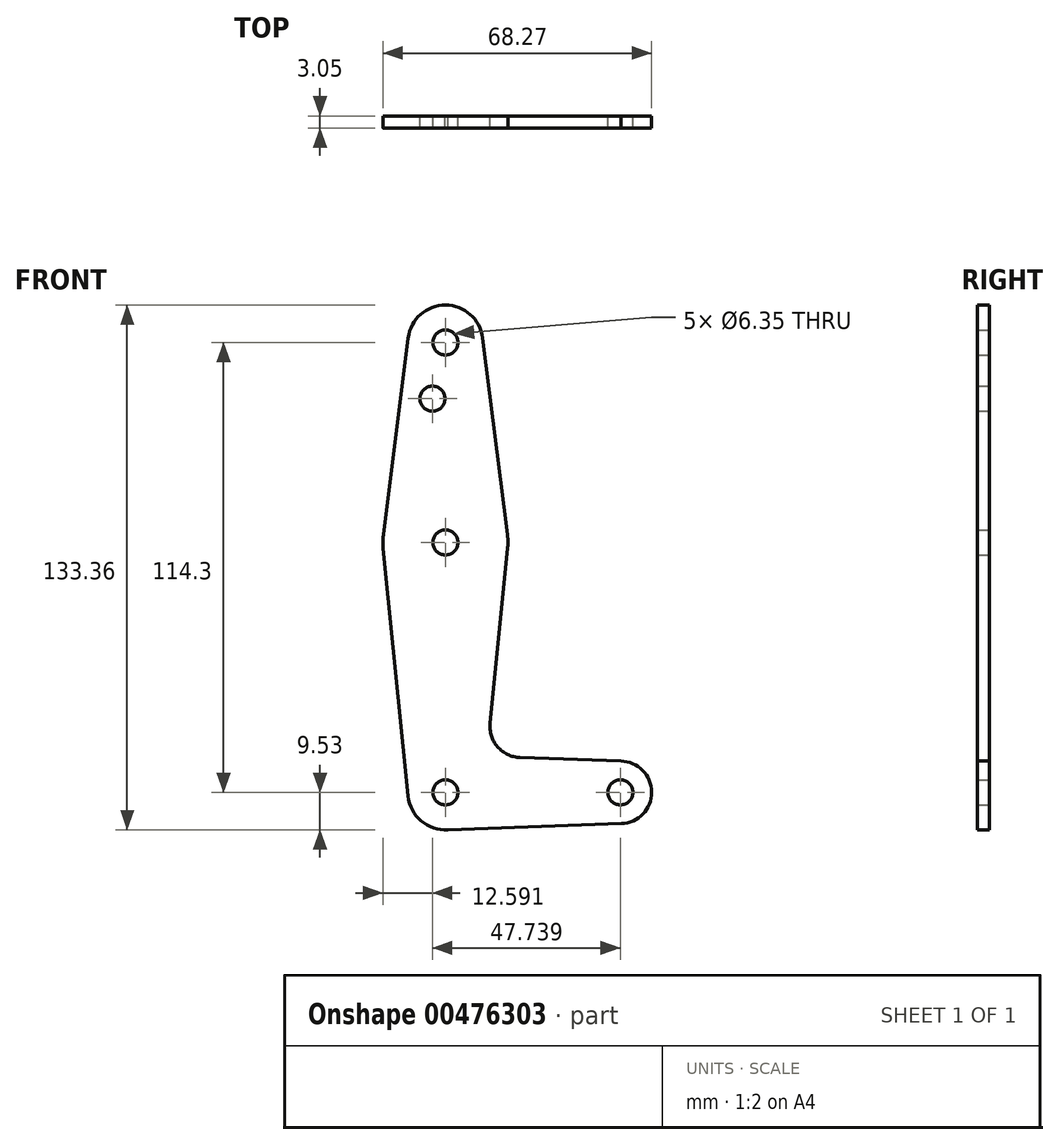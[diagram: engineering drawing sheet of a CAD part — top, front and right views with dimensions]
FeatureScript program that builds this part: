
annotation { "Feature Type Name" : "Feature", "Feature Type Description" : "" }
export const myFeature = defineFeature(function(context is Context, id is Id, definition is map)
    precondition{}
    {
        {
            var Q0;
            Q0=qCreatedBy(makeId("Front.planeOp"),FACE);
            var sketch = newSketch(context, id + "F0", { "sketchPlane" : qUnion([Q0])});
            skLineSegment(sketch, "E0", {"start": v(0, 114.3) * mm, "end": v(0, 0) * mm, "construction": true});
            skLineSegment(sketch, "E1", {"start": v(0, 0) * mm, "end": v(44.45, 0) * mm, "construction": true});
            skCircle(sketch, "E2", {"center": v(0, 114.3) * mm, "radius": 9.53 * mm});
            skCircle(sketch, "E3", {"center": v(0, 63.5) * mm, "radius": 15.88 * mm});
            skCircle(sketch, "E4", {"center": v(0, 0) * mm, "radius": 9.53 * mm});
            skCircle(sketch, "E5", {"center": v(44.45, 0) * mm, "radius": 7.94 * mm});
            skLineSegment(sketch, "E6", {"start": v(15.75, 65.48) * mm, "end": v(9.45, 115.5) * mm});
            skLineSegment(sketch, "E7", {"start": v(-15.75, 65.48) * mm, "end": v(-9.45, 115.5) * mm});
            skCircle(sketch, "E8", {"center": v(0, 114.3) * mm, "radius": 3.18 * mm});
            skCircle(sketch, "E9", {"center": v(0, 63.5) * mm, "radius": 3.18 * mm});
            skCircle(sketch, "E10", {"center": v(0, 0) * mm, "radius": 3.18 * mm});
            skCircle(sketch, "E11", {"center": v(44.45, 0) * mm, "radius": 3.18 * mm});
            skCircle(sketch, "E12", {"center": v(-3.29, 100.03) * mm, "radius": 3.18 * mm});
            skLineSegment(sketch, "E13", {"start": v(-15.8, 61.91) * mm, "end": v(-9.48, -0.95) * mm});
            skLineSegment(sketch, "E14", {"start": v(11.34, 17.6) * mm, "end": v(15.8, 61.91) * mm});
            skLineSegment(sketch, "E15", {"start": v(0.63, -9.5) * mm, "end": v(44.73, -7.93) * mm});
            skLineSegment(sketch, "E16", {"start": v(44.56, 7.94) * mm, "end": v(18.97, 8.85) * mm});
            skArc(sketch, "E17.filletArc", {"start": v(11.34, 17.6) * mm, "mid": v(13.26, 11.57) * mm, "end": v(18.97, 8.85) * mm});
            skSolve(sketch);
        }
        {
            var Q0;
            Q0 = qSketchRegion(id + "F0", true);
            extrude(context, id + "F1", {"entities" : qUnion([Q0]), "depth" : 3.05 * mm});
        }
    });
